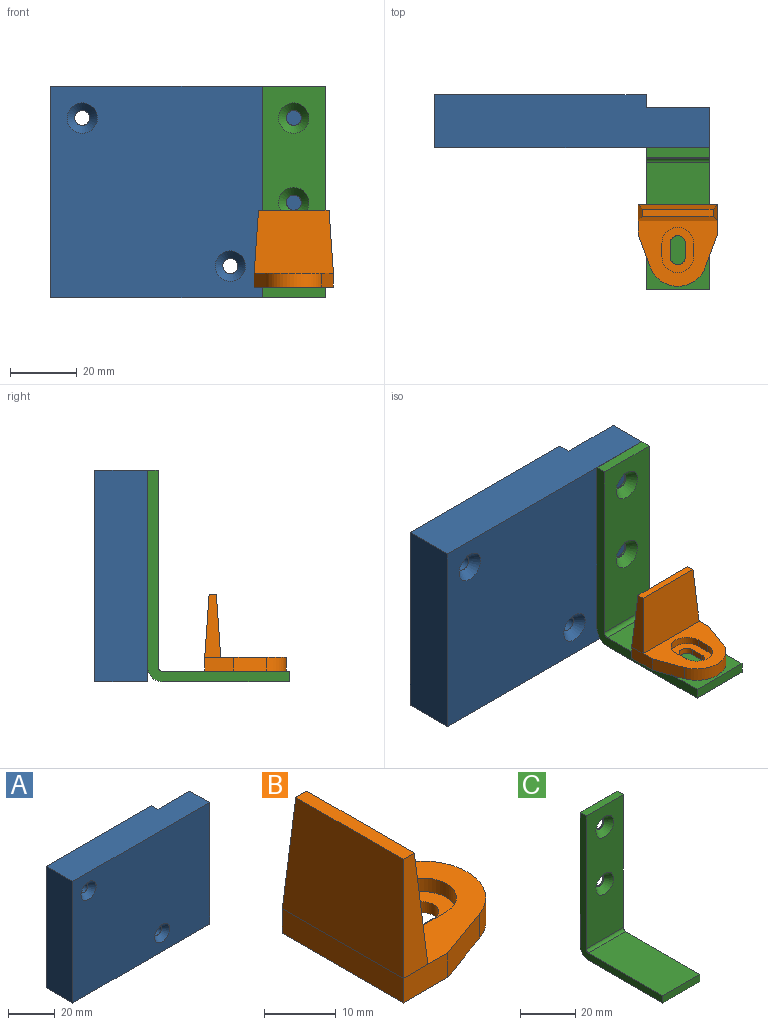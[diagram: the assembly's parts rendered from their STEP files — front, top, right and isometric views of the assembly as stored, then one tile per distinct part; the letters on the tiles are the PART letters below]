
ASSEMBLY  parts=3 mates=2
PART A: 12 faces, bbox 82.6x15.9x63.5 mm
  f0: plane 82.55x15.88mm, normal (0,0,1), area 1237.9mm2, adj f1,f3,f4,f5,f6,f7
  f1: plane 63.5x15.88mm, normal (-1,0,0), area 1008.1mm2, adj f0,f2,f4,f5
  f2: plane 82.55x15.88mm, normal (0,0,-1), area 1237.9mm2, adj f1,f3,f4,f5,f6,f7
  f3: plane 63.5x12.07mm, normal (1,0,0), area 766.1mm2, adj f0,f2,f4,f7
  f4: plane 82.55x63.5mm, normal (0,-1,0), area 5111.3mm2, adj f0,f1,f2,f3,f9,f11
  f5: plane 63.5x63.5mm, normal (0,1,0), area 4000.5mm2, adj f0,f1,f2,f6,f8,f10
  f6: plane 63.5x3.81mm, normal (1,0,0), area 241.9mm2, adj f0,f2,f5,f7
  f7: plane 63.5x19.05mm, normal (0,1,0), area 1209.7mm2, adj f0,f2,f3,f6
  f8: cylinder r=2.25mm len=13.22mm, axis (0,-1,0), area 186.7mm2, adj f5,f9
  f9: cone r=2.25mm half-angle=41deg, axis (0,-1,0), area 75.3mm2, adj f4,f8
  f10: cylinder r=2.25mm len=13.22mm, axis (0,-1,0), area 186.7mm2, adj f5,f11
  f11: cone r=2.25mm half-angle=41deg, axis (0,-1,0), area 75.3mm2, adj f4,f10
PART B: 22 faces, bbox 24.5x23.8x23.1 mm
  f0: plane 8.76x4.17mm, normal (0,1,0), area 36.5mm2, adj f1,f2,f3,f7,f21
  f1: plane 24.47x23.83mm, normal (0,0,-1), area 444mm2, adj f0,f3,f4,f5,f6,f17,f18,f19
  f2: plane 23.83x19.65mm, normal (0,0,1), area 254.3mm2, adj f0,f3,f4,f5,f6,f10,f12,f13
  f3: plane 9.89x4.17mm, normal (0.34,0.94,0), area 43.8mm2, adj f0,f1,f2,f4
  f4: cylinder r=8.85mm len=16.63mm, axis (0,0,-1), area 90mm2, adj f1,f2,f3,f6
  f5: plane 8.76x4.17mm, normal (0,-1,0), area 36.5mm2, adj f1,f2,f6,f9,f21
  f6: plane 9.89x4.17mm, normal (0.34,-0.94,0), area 43.8mm2, adj f1,f2,f4,f5
  f7: plane 18.97x4.83mm, normal (0,1,0.07), area 66.6mm2, adj f0,f8,f10,f11
  f8: plane 23.83x18.97mm, normal (-1,0,0.07), area 427.9mm2, adj f7,f9,f11,f21
  f9: plane 18.97x4.83mm, normal (0,-1,0.07), area 66.6mm2, adj f5,f8,f10,f11
  f10: plane 23.83x18.97mm, normal (1,0,0.07), area 427.9mm2, adj f2,f7,f9,f11
  f11: plane 21.17x2.17mm, normal (0,0,1), area 46mm2, adj f7,f8,f9,f10
  f12: plane 4.06x2.31mm, normal (0,-1,0), area 9.4mm2, adj f2,f13,f15,f16
  f13: cylinder r=4.76mm len=9.53mm, axis (0,0,1), area 34.6mm2, adj f2,f12,f14,f16
  f14: plane 4.06x2.31mm, normal (0,1,0), area 9.4mm2, adj f2,f13,f15,f16
  f15: cylinder r=4.76mm len=9.53mm, axis (0,0,1), area 34.6mm2, adj f2,f12,f14,f16
  f16: plane 13.59x9.53mm, normal (0,0,1), area 74.7mm2, adj f12,f13,f14,f15,f17,f18,f19,f20
  f17: plane 4.06x1.85mm, normal (0,1,0), area 7.5mm2, adj f1,f16,f18,f20
  f18: cylinder r=2.3mm len=4.6mm, axis (0,0,1), area 13.4mm2, adj f1,f16,f17,f19
  f19: plane 4.06x1.85mm, normal (0,-1,0), area 7.5mm2, adj f1,f16,f18,f20
  f20: cylinder r=2.3mm len=4.6mm, axis (0,0,1), area 13.4mm2, adj f1,f16,f17,f19
  f21: plane 23.83x4.17mm, normal (-1,0,0), area 99.2mm2, adj f0,f1,f5,f8
PART C: 14 faces, bbox 19.1x42.5x63.5 mm
  f0: cylinder r=4.45mm len=19.05mm, axis (-1,0,0), area 133mm2, adj f1,f7,f8,f9
  f1: plane 59.06x19.05mm, normal (0,1,0), area 1093.2mm2, adj f0,f2,f8,f9,f10,f12
  f2: plane 19.05x3.18mm, normal (0,0,1), area 60.5mm2, adj f1,f3,f8,f9
  f3: plane 59.06x19.05mm, normal (0,-1,0), area 994.4mm2, adj f2,f4,f8,f9,f11,f13
  f4: cylinder r=1.27mm len=19.05mm, axis (-1,0,0), area 38mm2, adj f3,f5,f8,f9
  f5: plane 38.1x19.05mm, normal (0,0,1), area 725.8mm2, adj f4,f6,f8,f9
  f6: plane 19.05x3.18mm, normal (0,-1,0), area 60.5mm2, adj f5,f7,f8,f9
  f7: plane 38.1x19.05mm, normal (0,0,-1), area 725.8mm2, adj f0,f6,f8,f9
  f8: plane 63.5x42.55mm, normal (1,0,0), area 322.7mm2, adj f0,f1,f2,f3,f4,f5,f6,f7
  f9: plane 63.5x42.55mm, normal (-1,0,0), area 322.7mm2, adj f0,f1,f2,f3,f4,f5,f6,f7
  f10: cylinder r=2.25mm len=4.5mm, axis (0,-1,0), area 7.3mm2, adj f1,f11
  f11: cone r=2.25mm half-angle=41deg, axis (0,-1,0), area 75.3mm2, adj f3,f10
  f12: cylinder r=2.25mm len=4.5mm, axis (0,-1,0), area 7.3mm2, adj f1,f13
  f13: cone r=2.25mm half-angle=41deg, axis (0,-1,0), area 75.3mm2, adj f3,f12
PLACE A t=(-86.64,-3.05,-21.01)mm
PLACE B rot(axis=(0,0,-1),90deg) t=(-45.37,-38.49,-49.58)mm
PLACE C t=(-45.37,-42.42,-49.58)mm
MATE fastened B.f1 <-> C.f5  axis (0,0,-1) through (-45.37,-36.07,-49.58)mm
MATE fastened A.f4 <-> C.f1  axis (0,-1,0) through (-35.84,-18.93,10.74)mm
